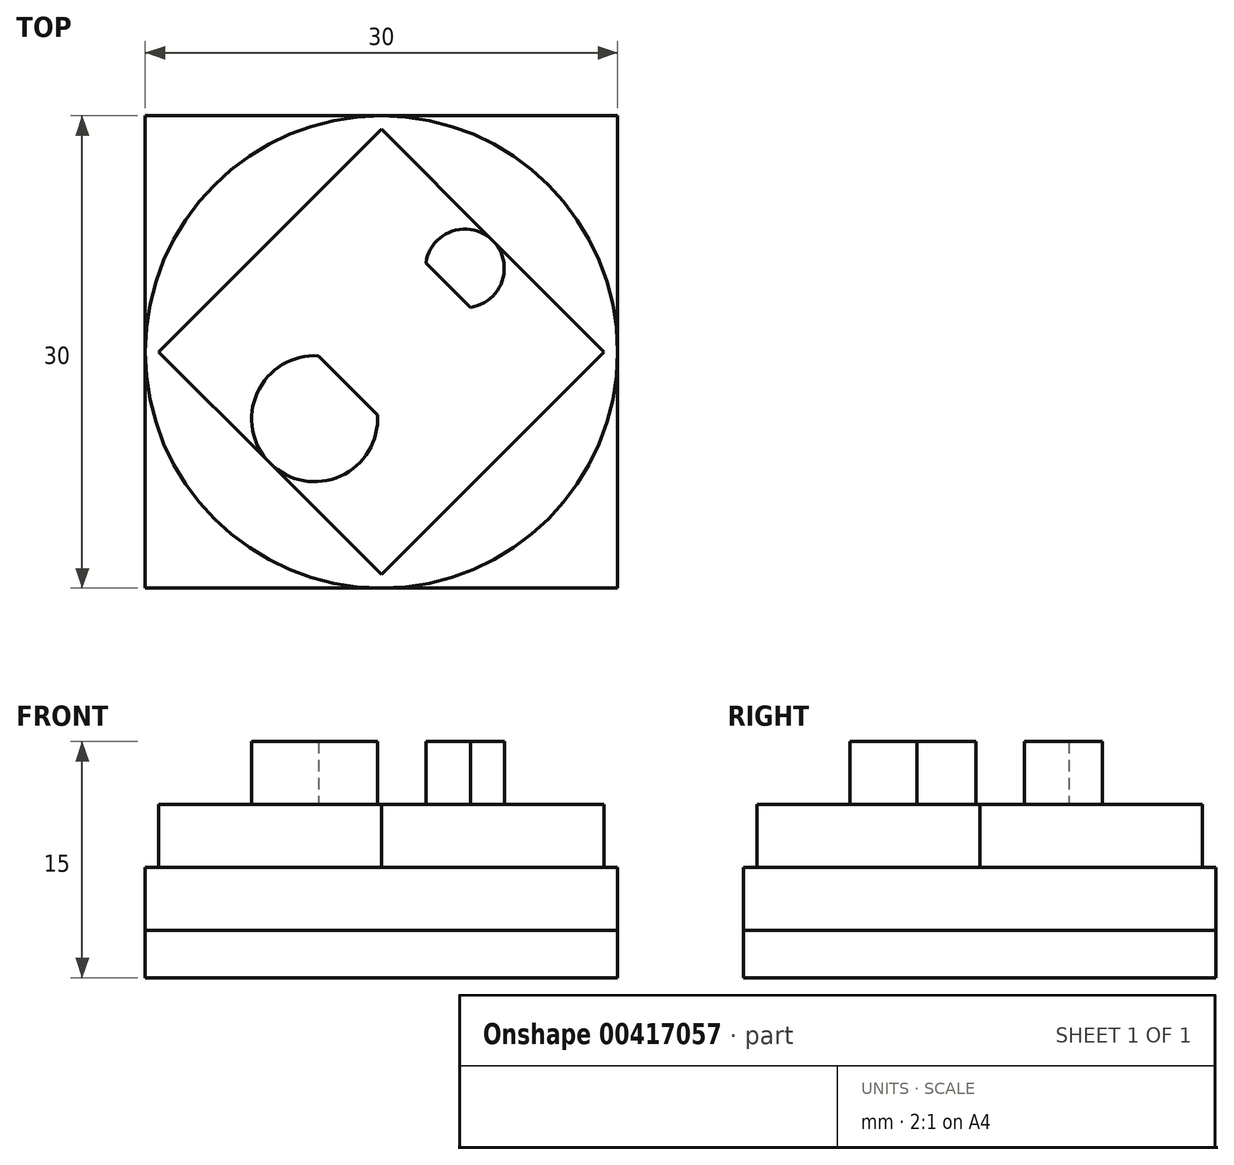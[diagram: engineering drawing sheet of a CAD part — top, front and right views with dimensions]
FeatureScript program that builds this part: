
annotation { "Feature Type Name" : "Feature", "Feature Type Description" : "" }
export const myFeature = defineFeature(function(context is Context, id is Id, definition is map)
    precondition{}
    {
        {
            var Q0;
            Q0=qCreatedBy(makeId("Top.planeOp"),FACE);
            var sketch = newSketch(context, id + "F0", { "sketchPlane" : qUnion([Q0])});
            skLineSegment(sketch, "E0.bottom", {"start": v(15, -15) * mm, "end": v(-15, -15) * mm});
            skLineSegment(sketch, "E0.top", {"start": v(15, 15) * mm, "end": v(-15, 15) * mm});
            skLineSegment(sketch, "E0.left", {"start": v(15, -15) * mm, "end": v(15, 15) * mm});
            skLineSegment(sketch, "E0.right", {"start": v(-15, -15) * mm, "end": v(-15, 15) * mm});
            skPoint(sketch, "E0.middle", {"position": v(0, 0) * mm});
            skSolve(sketch);
        }
        {
            var Q0;
            Q0 = qSketchRegion(id + "F0", true);
            extrude(context, id + "F1", {"entities" : qUnion([Q0]), "depth" : 3 * mm});
        }
        {
            var Q0;
            Q0=makeQuery(id+"F1.opExtrude","CAP_FACE",FACE,{"disambiguationData":[OSD([sQuery(id+"F0.wireOp",EDGE,"E0.bottom"),sQuery(id+"F0.wireOp",EDGE,"E0.top"),sQuery(id+"F0.wireOp",EDGE,"E0.left"),sQuery(id+"F0.wireOp",EDGE,"E0.right")])],"isStart":false});
            var sketch = newSketch(context, id + "F2", { "sketchPlane" : qUnion([Q0])});
            skCircle(sketch, "E1", {"center": v(0, 0) * mm, "radius": 15 * mm});
            skSolve(sketch);
        }
        {
            var Q0;
            Q0 = qSketchRegion(id + "F2", true);
            extrude(context, id + "F3", {"entities" : qUnion([Q0]), "operationType" : NewBodyOperationType.ADD, "depth" : 4 * mm});
        }
        {
            var Q0;
            Q0=makeQuery(id+"F3.opExtrude","CAP_FACE",FACE,{"disambiguationData":[OSD([sQuery(id+"F2.wireOp",EDGE,"E1")])],"isStart":false});
            var sketch = newSketch(context, id + "F4", { "sketchPlane" : qUnion([Q0])});
            skLineSegment(sketch, "E2", {"start": v(0, 14.14) * mm, "end": v(-14.14, 0) * mm});
            skLineSegment(sketch, "E3", {"start": v(-14.14, 0) * mm, "end": v(0, -14.14) * mm});
            skLineSegment(sketch, "E4", {"start": v(0, -14.14) * mm, "end": v(14.14, 0) * mm});
            skLineSegment(sketch, "E5", {"start": v(14.14, 0) * mm, "end": v(0, 14.14) * mm});
            skSolve(sketch);
        }
        {
            var Q0;
            Q0 = qSketchRegion(id + "F4", true);
            var Q1;
            Q1 = qSketchRegion(id + "F6", true);
            extrude(context, id + "F5", {"entities" : qUnion([Q0, Q1]), "operationType" : NewBodyOperationType.ADD, "depth" : 4 * mm});
        }
        {
            var Q0;
            Q0=makeQuery(id+"F5.opExtrude","CAP_FACE",FACE,{"disambiguationData":[OSD([sQuery(id+"F4.wireOp",EDGE,"E2"),sQuery(id+"F4.wireOp",EDGE,"E3"),sQuery(id+"F4.wireOp",EDGE,"E4"),sQuery(id+"F4.wireOp",EDGE,"E5")])],"isStart":false});
            var sketch = newSketch(context, id + "F6", { "sketchPlane" : qUnion([Q0])});
            skLineSegment(sketch, "E6", {"start": v(7.07, 7.07) * mm, "end": v(-7.07, -7.07) * mm, "construction": true});
            skArc(sketch, "E7", {"start": v(5.66, 2.83) * mm, "mid": v(7.07, 7.07) * mm, "end": v(2.83, 5.66) * mm});
            skArc(sketch, "E8", {"start": v(-4, -0.25) * mm, "mid": v(-7.07, -7.07) * mm, "end": v(-0.25, -4) * mm});
            skLineSegment(sketch, "E9", {"start": v(2.83, 5.66) * mm, "end": v(5.66, 2.83) * mm});
            skLineSegment(sketch, "E10", {"start": v(-4, -0.25) * mm, "end": v(-0.25, -4) * mm});
            skSolve(sketch);
        }
        {
            var Q0;
            Q0 = qSketchRegion(id + "F6", true);
            extrude(context, id + "F7", {"entities" : qUnion([Q0]), "operationType" : NewBodyOperationType.ADD, "depth" : 4 * mm});
        }
    });
